# Revit family: Spiralrohrabhänger, schallgedämmt
name_source: partatom
category: HLS-Bauteile
revit_build: Autodesk Revit 2017 (Build: 20190507_1515(x64)
units: mm (PartAtom-declared; Revit-internal decimal feet)

## family parameters
Arbeitsebenenbasiert = Ja
Beim Laden mit Abzugskörper schneiden = Nein
Bemaßung runder Anschluss = Durchmesser verwenden
Gemeinsam genutzt = Ja
Immer vertikal = Nein
Raumberechnungspunkt = Nein
Teiletyp = Normal

## types (1)
- Spiralrohrabhänger, schallgedämmt
    Anschluss = M8, M10
    Artikelnummer = 9998349
    EAN = 4250928446954
    Fabrikat = MEFA
    Firma = MEFA Befestigungs- und Montagesysteme GmbH
    Gewicht = 0.15 kg
    Gewicht pro Bauteil = 0.15 kg
    Kurztext1 = Spiralrohrabhänger schallgedämmt
    Kurztext2 = Gummi SBR Anschluss M8, M10
    Material = Stahl
    Materialmaße = 35 x 2,0 mm
    Materialname = S235
    Mengeneinheit = St
    Oberflaeche = galvanisch verzinkt
    Schalldämmeinlage = Gummi SBR
    Vorgabe-Ansicht = 1219 mm
    max. Temperaturbeständigkeit = 100 °C
    max. zul. Last = 0.90 kN
    vpe = 50 St
